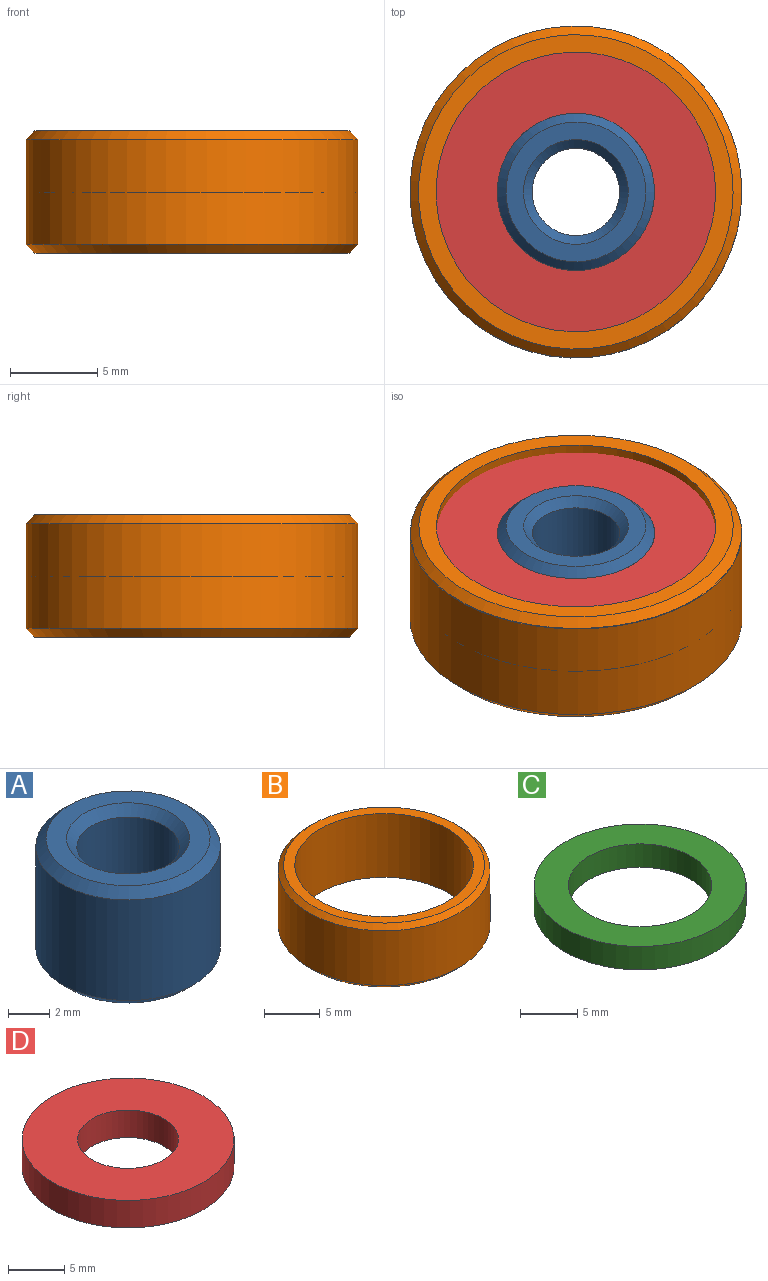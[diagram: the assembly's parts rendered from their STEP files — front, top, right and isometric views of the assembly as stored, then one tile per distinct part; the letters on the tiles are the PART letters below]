
ASSEMBLY  parts=4 mates=6
PART A: 8 faces, bbox 9x9x7 mm
  f0: cylinder r=2.5mm len=6mm, axis (0,0,-1), area 94.2mm2, adj f4,f6
  f1: cylinder r=4.5mm len=9mm, axis (0,0,-1), area 169.6mm2, adj f5,f7
  f2: plane 8x8mm, normal (0,0,1), area 22mm2, adj f6,f7
  f3: plane 8x8mm, normal (0,0,-1), area 22mm2, adj f4,f5
  f4: cone r=3mm half-angle=45deg, axis (0,0,-1), area 12.2mm2, adj f0,f3
  f5: cone r=4.5mm half-angle=45deg, axis (0,0,1), area 18.9mm2, adj f1,f3
  f6: cone r=2.5mm half-angle=45deg, axis (0,0,1), area 12.2mm2, adj f0,f2
  f7: cone r=4mm half-angle=45deg, axis (0,0,-1), area 18.9mm2, adj f1,f2
PART B: 6 faces, bbox 19x19x7 mm
  f0: cylinder r=8mm len=16mm, axis (0,0,-1), area 351.9mm2, adj f2,f3
  f1: cylinder r=9.5mm len=19mm, axis (0,0,-1), area 358.1mm2, adj f4,f5
  f2: plane 18x18mm, normal (0,0,1), area 53.4mm2, adj f0,f5
  f3: plane 18x18mm, normal (0,0,-1), area 53.4mm2, adj f0,f4
  f4: cone r=9.5mm half-angle=45deg, axis (0,0,1), area 41.1mm2, adj f1,f3
  f5: cone r=9mm half-angle=45deg, axis (0,0,-1), area 41.1mm2, adj f1,f2
PART C: 4 faces, bbox 18.5x18.5x2.5 mm
  f0: cylinder r=6.25mm len=12.5mm, axis (0,0,1), area 98.2mm2, adj f2,f3
  f1: cylinder r=9.25mm len=18.5mm, axis (0,0,1), area 145.3mm2, adj f2,f3
  f2: plane 18.5x18.5mm, normal (0,0,-1), area 146.1mm2, adj f0,f1
  f3: plane 18.5x18.5mm, normal (0,0,1), area 146.1mm2, adj f0,f1
PART D: 4 faces, bbox 18.9x18.9x3 mm
  f0: cylinder r=4.5mm len=9mm, axis (0,0,-1), area 84.8mm2, adj f2,f3
  f1: cylinder r=9.45mm len=18.9mm, axis (0,0,-1), area 178.1mm2, adj f2,f3
  f2: plane 18.9x18.9mm, normal (0,0,1), area 216.9mm2, adj f0,f1
  f3: plane 18.9x18.9mm, normal (0,0,-1), area 216.9mm2, adj f0,f1
PLACE A at identity fixed
PLACE B rot(axis=(0,0,-1),77.9deg) t=(0,0,0)mm
PLACE C rot(axis=(0,0,-1),77.9deg) t=(0,0,0.5)mm
PLACE D rot(axis=(0,0,1),90deg) t=(0,0,0)mm
MATE planar C.f1 <-> B.f1  axis (0,0,-1) through (0,0,-2)mm
MATE cylindrical A.f0 <-> D.f1  axis (0,0,-1) through (0,0,3)mm
MATE planar A.f1 <-> B.f1  axis (0,0,1) through (0,0,3.5)mm
MATE planar B.f1 <-> D.f1  axis (0,0,1) through (0,0,3.5)mm
MATE cylindrical A.f0 <-> B.f0  axis (0,0,-1) through (0,0,3)mm
MATE cylindrical C.f0 <-> B.f0  axis (0,0,1) through (0,0,0.5)mm
